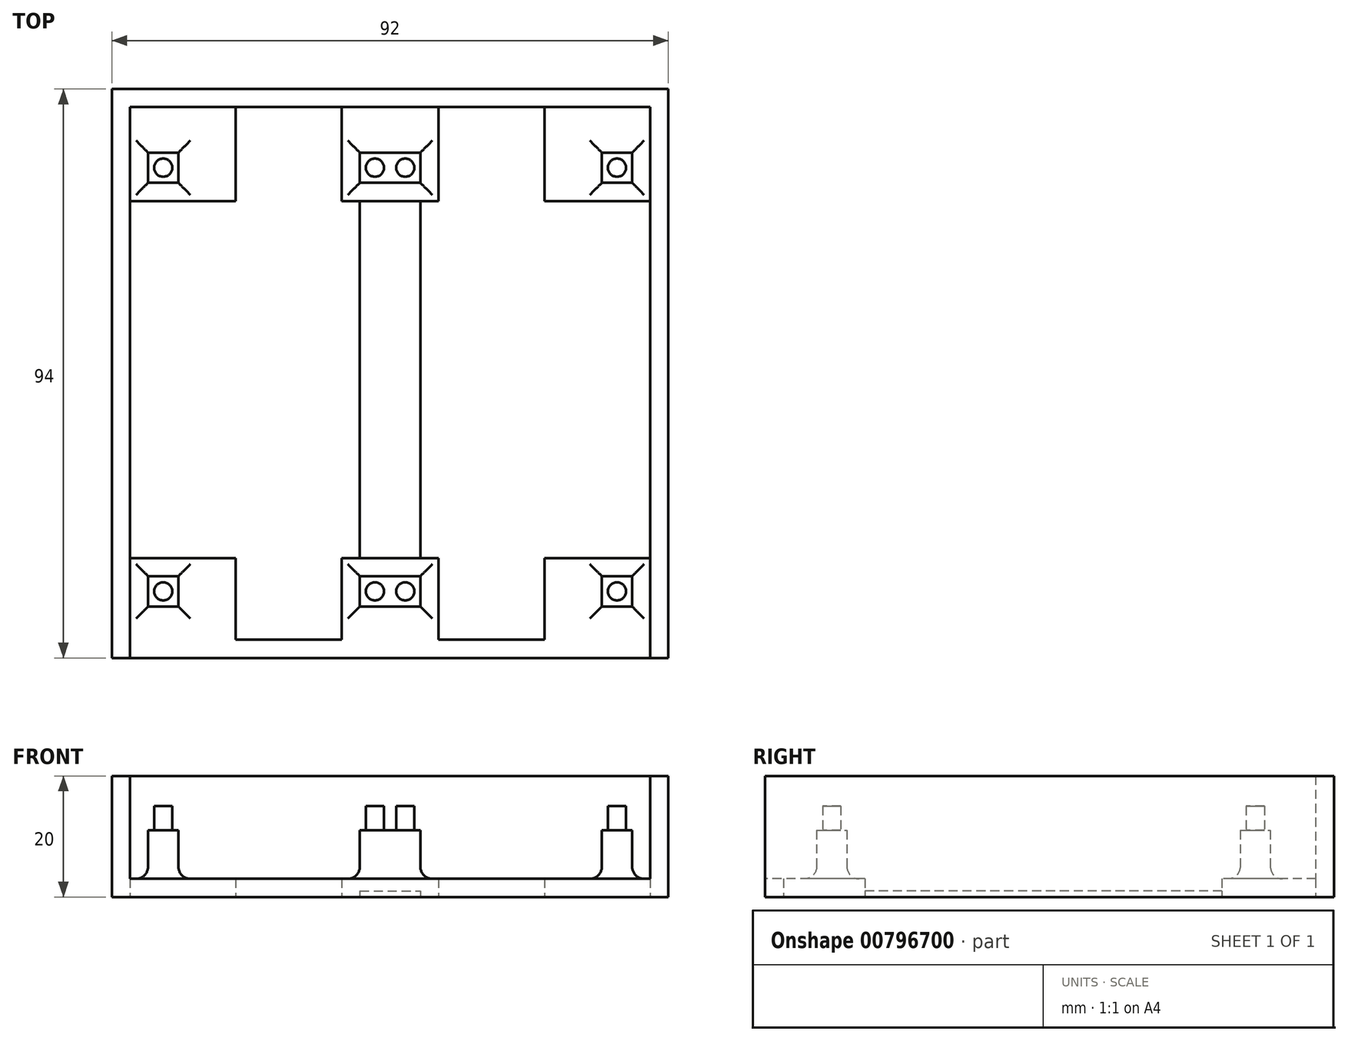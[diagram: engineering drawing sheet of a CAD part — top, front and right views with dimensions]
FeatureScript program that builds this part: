
annotation { "Feature Type Name" : "Feature", "Feature Type Description" : "" }
export const myFeature = defineFeature(function(context is Context, id is Id, definition is map)
    precondition{}
    {
        {
            var Q0;
            Q0=qCreatedBy(makeId("Top.planeOp"),FACE);
            var sketch = newSketch(context, id + "F0", { "sketchPlane" : qUnion([Q0])});
            skLineSegment(sketch, "E0.bottom", {"start": v(40, -41) * mm, "end": v(-40, -41) * mm, "construction": true});
            skLineSegment(sketch, "E0.top", {"start": v(40, 41) * mm, "end": v(-40, 41) * mm, "construction": true});
            skLineSegment(sketch, "E0.left", {"start": v(40, -41) * mm, "end": v(40, 41) * mm, "construction": true});
            skLineSegment(sketch, "E0.right", {"start": v(-40, -41) * mm, "end": v(-40, 41) * mm, "construction": true});
            skPoint(sketch, "E0.middle", {"position": v(0, 0) * mm});
            skLineSegment(sketch, "E1.bottom", {"start": v(-35, 31.5) * mm, "end": v(-40, 31.5) * mm});
            skLineSegment(sketch, "E1.top", {"start": v(-35, 36.5) * mm, "end": v(-40, 36.5) * mm});
            skLineSegment(sketch, "E1.left", {"start": v(-35, 31.5) * mm, "end": v(-35, 36.5) * mm});
            skLineSegment(sketch, "E1.right", {"start": v(-40, 31.5) * mm, "end": v(-40, 36.5) * mm});
            skPoint(sketch, "E1.middle", {"position": v(-37.5, 34) * mm});
            skLineSegment(sketch, "E2.bottom", {"start": v(-35, -38.5) * mm, "end": v(-40, -38.5) * mm});
            skLineSegment(sketch, "E2.top", {"start": v(-35, -33.5) * mm, "end": v(-40, -33.5) * mm});
            skLineSegment(sketch, "E2.left", {"start": v(-35, -38.5) * mm, "end": v(-35, -33.5) * mm});
            skLineSegment(sketch, "E2.right", {"start": v(-40, -38.5) * mm, "end": v(-40, -33.5) * mm});
            skPoint(sketch, "E2.middle", {"position": v(-37.5, -36) * mm});
            skLineSegment(sketch, "E3.bottom", {"start": v(40, -38.5) * mm, "end": v(35, -38.5) * mm});
            skLineSegment(sketch, "E3.top", {"start": v(40, -33.5) * mm, "end": v(35, -33.5) * mm});
            skLineSegment(sketch, "E3.left", {"start": v(40, -38.5) * mm, "end": v(40, -33.5) * mm});
            skLineSegment(sketch, "E3.right", {"start": v(35, -38.5) * mm, "end": v(35, -33.5) * mm});
            skPoint(sketch, "E3.middle", {"position": v(37.5, -36) * mm});
            skLineSegment(sketch, "E4.bottom", {"start": v(40, 31.5) * mm, "end": v(35, 31.5) * mm});
            skLineSegment(sketch, "E4.top", {"start": v(40, 36.5) * mm, "end": v(35, 36.5) * mm});
            skLineSegment(sketch, "E4.left", {"start": v(40, 31.5) * mm, "end": v(40, 36.5) * mm});
            skLineSegment(sketch, "E4.right", {"start": v(35, 31.5) * mm, "end": v(35, 36.5) * mm});
            skPoint(sketch, "E4.middle", {"position": v(37.5, 34) * mm});
            skLineSegment(sketch, "E5.bottom", {"start": v(0, 31.5) * mm, "end": v(-5, 31.5) * mm});
            skLineSegment(sketch, "E5.top", {"start": v(0, 36.5) * mm, "end": v(-5, 36.5) * mm});
            skLineSegment(sketch, "E5.left", {"start": v(0, 31.5) * mm, "end": v(0, 36.5) * mm});
            skLineSegment(sketch, "E5.right", {"start": v(-5, 31.5) * mm, "end": v(-5, 36.5) * mm});
            skPoint(sketch, "E5.middle", {"position": v(-2.5, 34) * mm});
            skLineSegment(sketch, "E6.bottom", {"start": v(0, -38.5) * mm, "end": v(-5, -38.5) * mm});
            skLineSegment(sketch, "E6.top", {"start": v(0, -33.5) * mm, "end": v(-5, -33.5) * mm});
            skLineSegment(sketch, "E6.left", {"start": v(0, -38.5) * mm, "end": v(0, -33.5) * mm});
            skLineSegment(sketch, "E6.right", {"start": v(-5, -38.5) * mm, "end": v(-5, -33.5) * mm});
            skPoint(sketch, "E6.middle", {"position": v(-2.5, -36) * mm});
            skLineSegment(sketch, "E7.bottom", {"start": v(5, -38.5) * mm, "end": v(0, -38.5) * mm});
            skLineSegment(sketch, "E7.top", {"start": v(5, -33.5) * mm, "end": v(0, -33.5) * mm});
            skLineSegment(sketch, "E7.left", {"start": v(5, -38.5) * mm, "end": v(5, -33.5) * mm});
            skPoint(sketch, "E7.middle", {"position": v(2.5, -36) * mm});
            skLineSegment(sketch, "E8", {"start": v(0, 41) * mm, "end": v(0, -41) * mm, "construction": true});
            skLineSegment(sketch, "E9.bottom", {"start": v(5, 31.5) * mm, "end": v(0, 31.5) * mm});
            skLineSegment(sketch, "E9.top", {"start": v(5, 36.5) * mm, "end": v(0, 36.5) * mm});
            skLineSegment(sketch, "E9.left", {"start": v(5, 31.5) * mm, "end": v(5, 36.5) * mm});
            skPoint(sketch, "E9.middle", {"position": v(2.5, 34) * mm});
            skPoint(sketch, "E9.middle.positionSnap0", {"position": v(0, 34) * mm});
            skPoint(sketch, "E9.centerSnap0", {"position": v(0, 34) * mm});
            skCircle(sketch, "E10", {"center": v(-37.5, 34) * mm, "radius": 1.5 * mm});
            skCircle(sketch, "E11", {"center": v(-2.5, 34) * mm, "radius": 1.5 * mm});
            skCircle(sketch, "E12", {"center": v(2.5, 34) * mm, "radius": 1.5 * mm});
            skCircle(sketch, "E13", {"center": v(37.5, 34) * mm, "radius": 1.5 * mm});
            skCircle(sketch, "E14", {"center": v(-37.5, -36) * mm, "radius": 1.5 * mm});
            skCircle(sketch, "E15", {"center": v(-2.5, -36) * mm, "radius": 1.5 * mm});
            skCircle(sketch, "E16", {"center": v(2.5, -36) * mm, "radius": 1.5 * mm});
            skCircle(sketch, "E17", {"center": v(37.5, -36) * mm, "radius": 1.5 * mm});
            skSolve(sketch);
        }
        {
            var Q0;
            Q0=qCreatedBy(makeId("Top.planeOp"),FACE);
            var sketch = newSketch(context, id + "F1", { "sketchPlane" : qUnion([Q0])});
            skLineSegment(sketch, "E18.0", {"start": v(40, 41) * mm, "end": v(-40, 41) * mm, "construction": true});
            skLineSegment(sketch, "E19.0", {"start": v(-40, -41) * mm, "end": v(-40, 41) * mm, "construction": true});
            skLineSegment(sketch, "E20.0", {"start": v(40, -41) * mm, "end": v(40, 41) * mm, "construction": true});
            skLineSegment(sketch, "E21.0", {"start": v(40, -41) * mm, "end": v(-40, -41) * mm, "construction": true});
            skLineSegment(sketch, "E22.bottom", {"start": v(43, -44) * mm, "end": v(-43, -44) * mm});
            skLineSegment(sketch, "E22.top", {"start": v(43, 44) * mm, "end": v(-43, 44) * mm});
            skLineSegment(sketch, "E22.left", {"start": v(43, -44) * mm, "end": v(43, 44) * mm});
            skLineSegment(sketch, "E22.right", {"start": v(-43, -44) * mm, "end": v(-43, 44) * mm});
            skPoint(sketch, "E22.middle", {"position": v(0, 0) * mm});
            skLineSegment(sketch, "E23.bottom", {"start": v(46, -47) * mm, "end": v(-46, -47) * mm});
            skLineSegment(sketch, "E23.top", {"start": v(46, 47) * mm, "end": v(-46, 47) * mm});
            skLineSegment(sketch, "E23.left", {"start": v(46, -47) * mm, "end": v(46, 47) * mm});
            skLineSegment(sketch, "E23.right", {"start": v(-46, -47) * mm, "end": v(-46, 47) * mm});
            skLineSegment(sketch, "E24", {"start": v(-43, -44) * mm, "end": v(-43, -47) * mm});
            skLineSegment(sketch, "E25", {"start": v(43, -44) * mm, "end": v(43, -47) * mm});
            skPoint(sketch, "E26.0", {"position": v(-37.5, 31.5) * mm});
            skPoint(sketch, "E27.0", {"position": v(-37.5, 36.5) * mm});
            skPoint(sketch, "E28.0", {"position": v(-37.5, -33.5) * mm});
            skPoint(sketch, "E29.0", {"position": v(-37.5, -38.5) * mm});
            skPoint(sketch, "E30.0", {"position": v(-5, 34) * mm});
            skPoint(sketch, "E31.0", {"position": v(5, 34) * mm});
            skLineSegment(sketch, "E32", {"start": v(-43, 31.5) * mm, "end": v(43, 31.5) * mm});
            skLineSegment(sketch, "E33", {"start": v(43, 36.5) * mm, "end": v(-43, 36.5) * mm});
            skLineSegment(sketch, "E34", {"start": v(-43, -33.5) * mm, "end": v(43, -33.5) * mm});
            skLineSegment(sketch, "E35", {"start": v(-43, -38.5) * mm, "end": v(43, -38.5) * mm});
            skLineSegment(sketch, "E36", {"start": v(-5, 44) * mm, "end": v(-5, -44) * mm});
            skLineSegment(sketch, "E37", {"start": v(5, 44) * mm, "end": v(5, -44) * mm});
            skLineSegment(sketch, "E38", {"start": v(-8, 44) * mm, "end": v(-8, -44) * mm});
            skLineSegment(sketch, "E39", {"start": v(8, 44) * mm, "end": v(8, -44) * mm});
            skLineSegment(sketch, "E40", {"start": v(-43, 28.5) * mm, "end": v(43, 28.5) * mm});
            skLineSegment(sketch, "E41", {"start": v(-43, -30.5) * mm, "end": v(43, -30.5) * mm});
            skPoint(sketch, "E42", {"position": v(-8, -30.5) * mm});
            skPoint(sketch, "E43", {"position": v(8, -30.5) * mm});
            skLineSegment(sketch, "E44", {"start": v(-8, -30.5) * mm, "end": v(-43, -30.5) * mm});
            skLineSegment(sketch, "E45", {"start": v(8, -30.5) * mm, "end": v(43, -30.5) * mm});
            skLineSegment(sketch, "E46", {"start": v(-25.5, -30.5) * mm, "end": v(-25.5, -44) * mm});
            skLineSegment(sketch, "E47", {"start": v(25.5, -30.5) * mm, "end": v(25.5, -44) * mm});
            skPoint(sketch, "E48", {"position": v(-8, 28.5) * mm});
            skPoint(sketch, "E49", {"position": v(8, 28.5) * mm});
            skLineSegment(sketch, "E50", {"start": v(-8, 28.5) * mm, "end": v(-43, 28.5) * mm});
            skLineSegment(sketch, "E51", {"start": v(8, 28.5) * mm, "end": v(43, 28.5) * mm});
            skLineSegment(sketch, "E52", {"start": v(-25.5, 28.5) * mm, "end": v(-25.5, 44) * mm});
            skLineSegment(sketch, "E53", {"start": v(25.5, 28.5) * mm, "end": v(25.5, 44) * mm});
            skLineSegment(sketch, "E54", {"start": v(-8, 28.5) * mm, "end": v(8, 28.5) * mm});
            skLineSegment(sketch, "E55", {"start": v(-8, -30.5) * mm, "end": v(8, -30.5) * mm});
            skSolve(sketch);
        }
        {
            var Q0;
            {var subQ0=sQuery(id+"F1.wireOp",EDGE,"E36");var subQ1=sQuery(id+"F1.wireOp",EDGE,"E22.bottom");var subQ2=makeQuery(id+"F1.imprint","INTERSECT",VERTEX,{"derivedFrom":[subQ1,subQ0]});Q0=makeQuery(id+"F1.imprint","IMPRINT",FACE,{"disambiguationData":[TD([[makeQuery(id+"F1.imprint","IMPRINT",EDGE,{"disambiguationData":[TD([[subQ2,-1.0]])],"derivedFrom":subQ1}),-1.0]])]});}
            var Q1;
            {var subQ0=sQuery(id+"F1.wireOp",EDGE,"E36");var subQ1=sQuery(id+"F1.wireOp",EDGE,"E22.top");var subQ2=makeQuery(id+"F1.imprint","INTERSECT",VERTEX,{"derivedFrom":[subQ1,subQ0]});Q1=makeQuery(id+"F1.imprint","IMPRINT",FACE,{"disambiguationData":[TD([[makeQuery(id+"F1.imprint","IMPRINT",EDGE,{"disambiguationData":[TD([[subQ2,-1.0]])],"derivedFrom":subQ1}),1.0]])]});}
            var Q2;
            {var subQ0=sQuery(id+"F1.wireOp",EDGE,"E38");var subQ1=sQuery(id+"F1.wireOp",EDGE,"E32");var subQ2=makeQuery(id+"F1.imprint","INTERSECT",VERTEX,{"derivedFrom":[subQ1,subQ0]});Q2=makeQuery(id+"F1.imprint","IMPRINT",FACE,{"disambiguationData":[TD([[makeQuery(id+"F1.imprint","IMPRINT",EDGE,{"disambiguationData":[TD([[subQ2,-1.0]])],"derivedFrom":subQ1}),1.0]])]});}
            var Q3;
            {var subQ0=sQuery(id+"F1.wireOp",EDGE,"E38");var subQ1=sQuery(id+"F1.wireOp",EDGE,"E32");var subQ2=makeQuery(id+"F1.imprint","INTERSECT",VERTEX,{"derivedFrom":[subQ1,subQ0]});Q3=makeQuery(id+"F1.imprint","IMPRINT",FACE,{"disambiguationData":[TD([[makeQuery(id+"F1.imprint","IMPRINT",EDGE,{"disambiguationData":[TD([[subQ2,-1.0]])],"derivedFrom":subQ1}),-1.0]])]});}
            var Q4;
            {var subQ0=sQuery(id+"F1.wireOp",EDGE,"E38");var subQ1=sQuery(id+"F1.wireOp",EDGE,"E34");var subQ2=makeQuery(id+"F1.imprint","INTERSECT",VERTEX,{"derivedFrom":[subQ1,subQ0]});Q4=makeQuery(id+"F1.imprint","IMPRINT",FACE,{"disambiguationData":[TD([[makeQuery(id+"F1.imprint","IMPRINT",EDGE,{"disambiguationData":[TD([[subQ2,-1.0]])],"derivedFrom":subQ1}),-1.0]])]});}
            var Q5;
            {var subQ0=sQuery(id+"F1.wireOp",EDGE,"E38");var subQ1=sQuery(id+"F1.wireOp",EDGE,"E34");var subQ2=makeQuery(id+"F1.imprint","INTERSECT",VERTEX,{"derivedFrom":[subQ1,subQ0]});Q5=makeQuery(id+"F1.imprint","IMPRINT",FACE,{"disambiguationData":[TD([[makeQuery(id+"F1.imprint","IMPRINT",EDGE,{"disambiguationData":[TD([[subQ2,-1.0]])],"derivedFrom":subQ1}),1.0]])]});}
            var Q6;
            {var subQ6=sQuery(id+"F1.wireOp",EDGE,"E24");Q6=makeQuery(id+"F1.imprint","IMPRINT",FACE,{"disambiguationData":[TD([[makeQuery(id+"F1.imprint","IMPRINT",EDGE,{"derivedFrom":subQ6}),1.0]])]});}
            var Q7;
            Q7=makeQuery(id+"F1.imprint","IMPRINT",FACE,{"disambiguationData":[TD([[makeQuery(id+"F1.imprint","IMPRINT",EDGE,{"derivedFrom":sQuery(id+"F1.wireOp",EDGE,"E23.top")}),1.0]])]});
            var Q8;
            {var subQ0=sQuery(id+"F1.wireOp",EDGE,"E22.right");var subQ1=sQuery(id+"F1.wireOp",EDGE,"E22.top");var subQ2=makeQuery(id+"F1.imprint","INTERSECT",VERTEX,{"derivedFrom":[subQ1,subQ0]});Q8=makeQuery(id+"F1.imprint","IMPRINT",FACE,{"disambiguationData":[TD([[makeQuery(id+"F1.imprint","IMPRINT",EDGE,{"disambiguationData":[TD([[subQ2,1.0]])],"derivedFrom":subQ1}),1.0]])]});}
            var Q9;
            {var subQ0=sQuery(id+"F1.wireOp",EDGE,"E36");var subQ1=sQuery(id+"F1.wireOp",EDGE,"E22.top");var subQ2=makeQuery(id+"F1.imprint","INTERSECT",VERTEX,{"derivedFrom":[subQ1,subQ0]});Q9=makeQuery(id+"F1.imprint","IMPRINT",FACE,{"disambiguationData":[TD([[makeQuery(id+"F1.imprint","IMPRINT",EDGE,{"disambiguationData":[TD([[subQ2,1.0]])],"derivedFrom":subQ1}),1.0]])]});}
            var Q10;
            {var subQ0=sQuery(id+"F1.wireOp",EDGE,"E37");var subQ1=sQuery(id+"F1.wireOp",EDGE,"E22.top");var subQ2=makeQuery(id+"F1.imprint","INTERSECT",VERTEX,{"derivedFrom":[subQ1,subQ0]});Q10=makeQuery(id+"F1.imprint","IMPRINT",FACE,{"disambiguationData":[TD([[makeQuery(id+"F1.imprint","IMPRINT",EDGE,{"disambiguationData":[TD([[subQ2,1.0]])],"derivedFrom":subQ1}),1.0]])]});}
            var Q11;
            {var subQ0=sQuery(id+"F1.wireOp",EDGE,"E22.left");var subQ1=sQuery(id+"F1.wireOp",EDGE,"E22.top");var subQ2=makeQuery(id+"F1.imprint","INTERSECT",VERTEX,{"derivedFrom":[subQ1,subQ0]});Q11=makeQuery(id+"F1.imprint","IMPRINT",FACE,{"disambiguationData":[TD([[makeQuery(id+"F1.imprint","IMPRINT",EDGE,{"disambiguationData":[TD([[subQ2,-1.0]])],"derivedFrom":subQ1}),1.0]])]});}
            var Q12;
            {var subQ0=sQuery(id+"F1.wireOp",EDGE,"E32");var subQ1=sQuery(id+"F1.wireOp",EDGE,"E22.left");var subQ2=makeQuery(id+"F1.imprint","INTERSECT",VERTEX,{"derivedFrom":[subQ1,subQ0]});Q12=makeQuery(id+"F1.imprint","IMPRINT",FACE,{"disambiguationData":[TD([[makeQuery(id+"F1.imprint","IMPRINT",EDGE,{"disambiguationData":[TD([[subQ2,-1.0]])],"derivedFrom":subQ1}),1.0]])]});}
            var Q13;
            {var subQ0=sQuery(id+"F1.wireOp",EDGE,"E37");var subQ1=sQuery(id+"F1.wireOp",EDGE,"E32");var subQ2=makeQuery(id+"F1.imprint","INTERSECT",VERTEX,{"derivedFrom":[subQ1,subQ0]});Q13=makeQuery(id+"F1.imprint","IMPRINT",FACE,{"disambiguationData":[TD([[makeQuery(id+"F1.imprint","IMPRINT",EDGE,{"disambiguationData":[TD([[subQ2,-1.0]])],"derivedFrom":subQ1}),1.0]])]});}
            var Q14;
            {var subQ0=sQuery(id+"F1.wireOp",EDGE,"E32");var subQ1=sQuery(id+"F1.wireOp",EDGE,"E22.right");var subQ2=makeQuery(id+"F1.imprint","INTERSECT",VERTEX,{"derivedFrom":[subQ1,subQ0]});Q14=makeQuery(id+"F1.imprint","IMPRINT",FACE,{"disambiguationData":[TD([[makeQuery(id+"F1.imprint","IMPRINT",EDGE,{"disambiguationData":[TD([[subQ2,-1.0]])],"derivedFrom":subQ1}),-1.0]])]});}
            var Q15;
            {var subQ0=sQuery(id+"F1.wireOp",EDGE,"E36");var subQ1=sQuery(id+"F1.wireOp",EDGE,"E32");var subQ2=makeQuery(id+"F1.imprint","INTERSECT",VERTEX,{"derivedFrom":[subQ1,subQ0]});Q15=makeQuery(id+"F1.imprint","IMPRINT",FACE,{"disambiguationData":[TD([[makeQuery(id+"F1.imprint","IMPRINT",EDGE,{"disambiguationData":[TD([[subQ2,-1.0]])],"derivedFrom":subQ1}),1.0]])]});}
            var Q16;
            {var subQ0=sQuery(id+"F1.wireOp",EDGE,"E32");var subQ1=sQuery(id+"F1.wireOp",EDGE,"E22.right");var subQ2=makeQuery(id+"F1.imprint","INTERSECT",VERTEX,{"derivedFrom":[subQ1,subQ0]});Q16=makeQuery(id+"F1.imprint","IMPRINT",FACE,{"disambiguationData":[TD([[makeQuery(id+"F1.imprint","IMPRINT",EDGE,{"disambiguationData":[TD([[subQ2,1.0]])],"derivedFrom":subQ1}),-1.0]])]});}
            var Q17;
            {var subQ0=sQuery(id+"F1.wireOp",EDGE,"E37");var subQ1=sQuery(id+"F1.wireOp",EDGE,"E32");var subQ2=makeQuery(id+"F1.imprint","INTERSECT",VERTEX,{"derivedFrom":[subQ1,subQ0]});Q17=makeQuery(id+"F1.imprint","IMPRINT",FACE,{"disambiguationData":[TD([[makeQuery(id+"F1.imprint","IMPRINT",EDGE,{"disambiguationData":[TD([[subQ2,-1.0]])],"derivedFrom":subQ1}),-1.0]])]});}
            var Q18;
            {var subQ0=sQuery(id+"F1.wireOp",EDGE,"E32");var subQ1=sQuery(id+"F1.wireOp",EDGE,"E22.left");var subQ2=makeQuery(id+"F1.imprint","INTERSECT",VERTEX,{"derivedFrom":[subQ1,subQ0]});Q18=makeQuery(id+"F1.imprint","IMPRINT",FACE,{"disambiguationData":[TD([[makeQuery(id+"F1.imprint","IMPRINT",EDGE,{"disambiguationData":[TD([[subQ2,1.0]])],"derivedFrom":subQ1}),1.0]])]});}
            var Q19;
            {var subQ0=sQuery(id+"F1.wireOp",EDGE,"E36");var subQ1=sQuery(id+"F1.wireOp",EDGE,"E32");var subQ2=makeQuery(id+"F1.imprint","INTERSECT",VERTEX,{"derivedFrom":[subQ1,subQ0]});Q19=makeQuery(id+"F1.imprint","IMPRINT",FACE,{"disambiguationData":[TD([[makeQuery(id+"F1.imprint","IMPRINT",EDGE,{"disambiguationData":[TD([[subQ2,-1.0]])],"derivedFrom":subQ1}),-1.0]])]});}
            var Q20;
            {var subQ0=sQuery(id+"F1.wireOp",EDGE,"E36");var subQ1=sQuery(id+"F1.wireOp",EDGE,"E22.bottom");var subQ2=makeQuery(id+"F1.imprint","INTERSECT",VERTEX,{"derivedFrom":[subQ1,subQ0]});Q20=makeQuery(id+"F1.imprint","IMPRINT",FACE,{"disambiguationData":[TD([[makeQuery(id+"F1.imprint","IMPRINT",EDGE,{"disambiguationData":[TD([[subQ2,1.0]])],"derivedFrom":subQ1}),-1.0]])]});}
            var Q21;
            {var subQ0=sQuery(id+"F1.wireOp",EDGE,"E36");var subQ1=sQuery(id+"F1.wireOp",EDGE,"E34");var subQ2=makeQuery(id+"F1.imprint","INTERSECT",VERTEX,{"derivedFrom":[subQ1,subQ0]});Q21=makeQuery(id+"F1.imprint","IMPRINT",FACE,{"disambiguationData":[TD([[makeQuery(id+"F1.imprint","IMPRINT",EDGE,{"disambiguationData":[TD([[subQ2,-1.0]])],"derivedFrom":subQ1}),-1.0]])]});}
            var Q22;
            {var subQ0=sQuery(id+"F1.wireOp",EDGE,"E36");var subQ1=sQuery(id+"F1.wireOp",EDGE,"E34");var subQ2=makeQuery(id+"F1.imprint","INTERSECT",VERTEX,{"derivedFrom":[subQ1,subQ0]});Q22=makeQuery(id+"F1.imprint","IMPRINT",FACE,{"disambiguationData":[TD([[makeQuery(id+"F1.imprint","IMPRINT",EDGE,{"disambiguationData":[TD([[subQ2,-1.0]])],"derivedFrom":subQ1}),1.0]])]});}
            var Q23;
            {var subQ0=sQuery(id+"F1.wireOp",EDGE,"E37");var subQ1=sQuery(id+"F1.wireOp",EDGE,"E22.bottom");var subQ2=makeQuery(id+"F1.imprint","INTERSECT",VERTEX,{"derivedFrom":[subQ1,subQ0]});Q23=makeQuery(id+"F1.imprint","IMPRINT",FACE,{"disambiguationData":[TD([[makeQuery(id+"F1.imprint","IMPRINT",EDGE,{"disambiguationData":[TD([[subQ2,1.0]])],"derivedFrom":subQ1}),-1.0]])]});}
            var Q24;
            {var subQ0=sQuery(id+"F1.wireOp",EDGE,"E37");var subQ1=sQuery(id+"F1.wireOp",EDGE,"E34");var subQ2=makeQuery(id+"F1.imprint","INTERSECT",VERTEX,{"derivedFrom":[subQ1,subQ0]});Q24=makeQuery(id+"F1.imprint","IMPRINT",FACE,{"disambiguationData":[TD([[makeQuery(id+"F1.imprint","IMPRINT",EDGE,{"disambiguationData":[TD([[subQ2,-1.0]])],"derivedFrom":subQ1}),-1.0]])]});}
            var Q25;
            {var subQ0=sQuery(id+"F1.wireOp",EDGE,"E37");var subQ1=sQuery(id+"F1.wireOp",EDGE,"E34");var subQ2=makeQuery(id+"F1.imprint","INTERSECT",VERTEX,{"derivedFrom":[subQ1,subQ0]});Q25=makeQuery(id+"F1.imprint","IMPRINT",FACE,{"disambiguationData":[TD([[makeQuery(id+"F1.imprint","IMPRINT",EDGE,{"disambiguationData":[TD([[subQ2,-1.0]])],"derivedFrom":subQ1}),1.0]])]});}
            var Q26;
            {var subQ0=sQuery(id+"F1.wireOp",EDGE,"E34");var subQ1=sQuery(id+"F1.wireOp",EDGE,"E22.right");var subQ2=makeQuery(id+"F1.imprint","INTERSECT",VERTEX,{"derivedFrom":[subQ1,subQ0]});Q26=makeQuery(id+"F1.imprint","IMPRINT",FACE,{"disambiguationData":[TD([[makeQuery(id+"F1.imprint","IMPRINT",EDGE,{"disambiguationData":[TD([[subQ2,-1.0]])],"derivedFrom":subQ1}),-1.0]])]});}
            var Q27;
            {var subQ0=sQuery(id+"F1.wireOp",EDGE,"E34");var subQ1=sQuery(id+"F1.wireOp",EDGE,"E22.left");var subQ2=makeQuery(id+"F1.imprint","INTERSECT",VERTEX,{"derivedFrom":[subQ1,subQ0]});Q27=makeQuery(id+"F1.imprint","IMPRINT",FACE,{"disambiguationData":[TD([[makeQuery(id+"F1.imprint","IMPRINT",EDGE,{"disambiguationData":[TD([[subQ2,-1.0]])],"derivedFrom":subQ1}),1.0]])]});}
            var Q28;
            {var subQ0=sQuery(id+"F1.wireOp",EDGE,"E34");var subQ1=sQuery(id+"F1.wireOp",EDGE,"E22.left");var subQ2=makeQuery(id+"F1.imprint","INTERSECT",VERTEX,{"derivedFrom":[subQ1,subQ0]});Q28=makeQuery(id+"F1.imprint","IMPRINT",FACE,{"disambiguationData":[TD([[makeQuery(id+"F1.imprint","IMPRINT",EDGE,{"disambiguationData":[TD([[subQ2,1.0]])],"derivedFrom":subQ1}),1.0]])]});}
            var Q29;
            {var subQ0=sQuery(id+"F1.wireOp",EDGE,"E34");var subQ1=sQuery(id+"F1.wireOp",EDGE,"E22.right");var subQ2=makeQuery(id+"F1.imprint","INTERSECT",VERTEX,{"derivedFrom":[subQ1,subQ0]});Q29=makeQuery(id+"F1.imprint","IMPRINT",FACE,{"disambiguationData":[TD([[makeQuery(id+"F1.imprint","IMPRINT",EDGE,{"disambiguationData":[TD([[subQ2,1.0]])],"derivedFrom":subQ1}),-1.0]])]});}
            var Q30;
            {var subQ0=sQuery(id+"F1.wireOp",EDGE,"E22.right");var subQ5=sQuery(id+"F1.wireOp",EDGE,"E35");var subQ6=makeQuery(id+"F1.imprint","INTERSECT",VERTEX,{"derivedFrom":[subQ0,subQ5]});Q30=makeQuery(id+"F1.imprint","IMPRINT",FACE,{"disambiguationData":[TD([[makeQuery(id+"F1.imprint","IMPRINT",EDGE,{"disambiguationData":[TD([[subQ6,-1.0]])],"derivedFrom":subQ5}),-1.0]])]});}
            var Q31;
            {var subQ0=sQuery(id+"F1.wireOp",EDGE,"E22.left");var subQ5=sQuery(id+"F1.wireOp",EDGE,"E35");var subQ6=makeQuery(id+"F1.imprint","INTERSECT",VERTEX,{"derivedFrom":[subQ0,subQ5]});Q31=makeQuery(id+"F1.imprint","IMPRINT",FACE,{"disambiguationData":[TD([[makeQuery(id+"F1.imprint","IMPRINT",EDGE,{"disambiguationData":[TD([[subQ6,1.0]])],"derivedFrom":subQ5}),-1.0]])]});}
            extrude(context, id + "F2", {"entities" : qUnion([Q0, Q1, Q2, Q3, Q4, Q5, Q6, Q7, Q8, Q9, Q10, Q11, Q12, Q13, Q14, Q15, Q16, Q17, Q18, Q19, Q20, Q21, Q22, Q23, Q24, Q25, Q26, Q27, Q28, Q29, Q30, Q31]), "depth" : 3 * mm, "offsetDistance" : 25 * mm});
        }
        {
            var Q0;
            Q0=makeQuery(id+"F1.imprint","IMPRINT",FACE,{"disambiguationData":[TD([[makeQuery(id+"F1.imprint","IMPRINT",EDGE,{"derivedFrom":sQuery(id+"F1.wireOp",EDGE,"E23.top")}),1.0]])]});
            extrude(context, id + "F3", {"entities" : qUnion([Q0]), "operationType" : NewBodyOperationType.ADD, "depth" : 20 * mm, "offsetDistance" : 25 * mm});
        }
        {
            var Q0;
            Q0=makeQuery(id+"F0.imprint","IMPRINT",FACE,{"disambiguationData":[TD([[makeQuery(id+"F0.imprint","IMPRINT",EDGE,{"derivedFrom":sQuery(id+"F0.wireOp",EDGE,"E4.bottom")}),-1.0]])]});
            var Q1;
            Q1=makeQuery(id+"F0.imprint","IMPRINT",FACE,{"disambiguationData":[TD([[makeQuery(id+"F0.imprint","IMPRINT",EDGE,{"derivedFrom":sQuery(id+"F0.wireOp",EDGE,"E13")}),1.0]])]});
            var Q2;
            Q2=makeQuery(id+"F0.imprint","IMPRINT",FACE,{"disambiguationData":[TD([[makeQuery(id+"F0.imprint","IMPRINT",EDGE,{"derivedFrom":sQuery(id+"F0.wireOp",EDGE,"E9.bottom")}),-1.0]])]});
            var Q3;
            Q3=makeQuery(id+"F0.imprint","IMPRINT",FACE,{"disambiguationData":[TD([[makeQuery(id+"F0.imprint","IMPRINT",EDGE,{"derivedFrom":sQuery(id+"F0.wireOp",EDGE,"E12")}),1.0]])]});
            var Q4;
            Q4=makeQuery(id+"F0.imprint","IMPRINT",FACE,{"disambiguationData":[TD([[makeQuery(id+"F0.imprint","IMPRINT",EDGE,{"derivedFrom":sQuery(id+"F0.wireOp",EDGE,"E5.bottom")}),-1.0]])]});
            var Q5;
            Q5=makeQuery(id+"F0.imprint","IMPRINT",FACE,{"disambiguationData":[TD([[makeQuery(id+"F0.imprint","IMPRINT",EDGE,{"derivedFrom":sQuery(id+"F0.wireOp",EDGE,"E11")}),1.0]])]});
            var Q6;
            Q6=makeQuery(id+"F0.imprint","IMPRINT",FACE,{"disambiguationData":[TD([[makeQuery(id+"F0.imprint","IMPRINT",EDGE,{"derivedFrom":sQuery(id+"F0.wireOp",EDGE,"E1.bottom")}),-1.0]])]});
            var Q7;
            Q7=makeQuery(id+"F0.imprint","IMPRINT",FACE,{"disambiguationData":[TD([[makeQuery(id+"F0.imprint","IMPRINT",EDGE,{"derivedFrom":sQuery(id+"F0.wireOp",EDGE,"E10")}),1.0]])]});
            var Q8;
            Q8=makeQuery(id+"F0.imprint","IMPRINT",FACE,{"disambiguationData":[TD([[makeQuery(id+"F0.imprint","IMPRINT",EDGE,{"derivedFrom":sQuery(id+"F0.wireOp",EDGE,"E17")}),1.0]])]});
            var Q9;
            Q9=makeQuery(id+"F0.imprint","IMPRINT",FACE,{"disambiguationData":[TD([[makeQuery(id+"F0.imprint","IMPRINT",EDGE,{"derivedFrom":sQuery(id+"F0.wireOp",EDGE,"E3.bottom")}),-1.0]])]});
            var Q10;
            Q10=makeQuery(id+"F0.imprint","IMPRINT",FACE,{"disambiguationData":[TD([[makeQuery(id+"F0.imprint","IMPRINT",EDGE,{"derivedFrom":sQuery(id+"F0.wireOp",EDGE,"E6.bottom")}),-1.0]])]});
            var Q11;
            Q11=makeQuery(id+"F0.imprint","IMPRINT",FACE,{"disambiguationData":[TD([[makeQuery(id+"F0.imprint","IMPRINT",EDGE,{"derivedFrom":sQuery(id+"F0.wireOp",EDGE,"E15")}),1.0]])]});
            var Q12;
            Q12=makeQuery(id+"F0.imprint","IMPRINT",FACE,{"disambiguationData":[TD([[makeQuery(id+"F0.imprint","IMPRINT",EDGE,{"derivedFrom":sQuery(id+"F0.wireOp",EDGE,"E7.bottom")}),-1.0]])]});
            var Q13;
            Q13=makeQuery(id+"F0.imprint","IMPRINT",FACE,{"disambiguationData":[TD([[makeQuery(id+"F0.imprint","IMPRINT",EDGE,{"derivedFrom":sQuery(id+"F0.wireOp",EDGE,"E16")}),1.0]])]});
            var Q14;
            Q14=makeQuery(id+"F0.imprint","IMPRINT",FACE,{"disambiguationData":[TD([[makeQuery(id+"F0.imprint","IMPRINT",EDGE,{"derivedFrom":sQuery(id+"F0.wireOp",EDGE,"E2.bottom")}),-1.0]])]});
            var Q15;
            Q15=makeQuery(id+"F0.imprint","IMPRINT",FACE,{"disambiguationData":[TD([[makeQuery(id+"F0.imprint","IMPRINT",EDGE,{"derivedFrom":sQuery(id+"F0.wireOp",EDGE,"E14")}),1.0]])]});
            extrude(context, id + "F4", {"entities" : qUnion([Q0, Q1, Q2, Q3, Q4, Q5, Q6, Q7, Q8, Q9, Q10, Q11, Q12, Q13, Q14, Q15]), "operationType" : NewBodyOperationType.ADD, "depth" : 11 * mm, "offsetDistance" : 25 * mm});
        }
        {
            var Q0;
            Q0=makeQuery(id+"F0.imprint","IMPRINT",FACE,{"disambiguationData":[TD([[makeQuery(id+"F0.imprint","IMPRINT",EDGE,{"derivedFrom":sQuery(id+"F0.wireOp",EDGE,"E17")}),1.0]])]});
            var Q1;
            Q1=makeQuery(id+"F0.imprint","IMPRINT",FACE,{"disambiguationData":[TD([[makeQuery(id+"F0.imprint","IMPRINT",EDGE,{"derivedFrom":sQuery(id+"F0.wireOp",EDGE,"E16")}),1.0]])]});
            var Q2;
            Q2=makeQuery(id+"F0.imprint","IMPRINT",FACE,{"disambiguationData":[TD([[makeQuery(id+"F0.imprint","IMPRINT",EDGE,{"derivedFrom":sQuery(id+"F0.wireOp",EDGE,"E15")}),1.0]])]});
            var Q3;
            Q3=makeQuery(id+"F0.imprint","IMPRINT",FACE,{"disambiguationData":[TD([[makeQuery(id+"F0.imprint","IMPRINT",EDGE,{"derivedFrom":sQuery(id+"F0.wireOp",EDGE,"E14")}),1.0]])]});
            var Q4;
            Q4=makeQuery(id+"F0.imprint","IMPRINT",FACE,{"disambiguationData":[TD([[makeQuery(id+"F0.imprint","IMPRINT",EDGE,{"derivedFrom":sQuery(id+"F0.wireOp",EDGE,"E10")}),1.0]])]});
            var Q5;
            Q5=makeQuery(id+"F0.imprint","IMPRINT",FACE,{"disambiguationData":[TD([[makeQuery(id+"F0.imprint","IMPRINT",EDGE,{"derivedFrom":sQuery(id+"F0.wireOp",EDGE,"E11")}),1.0]])]});
            var Q6;
            Q6=makeQuery(id+"F0.imprint","IMPRINT",FACE,{"disambiguationData":[TD([[makeQuery(id+"F0.imprint","IMPRINT",EDGE,{"derivedFrom":sQuery(id+"F0.wireOp",EDGE,"E12")}),1.0]])]});
            var Q7;
            Q7=makeQuery(id+"F0.imprint","IMPRINT",FACE,{"disambiguationData":[TD([[makeQuery(id+"F0.imprint","IMPRINT",EDGE,{"derivedFrom":sQuery(id+"F0.wireOp",EDGE,"E13")}),1.0]])]});
            extrude(context, id + "F5", {"entities" : qUnion([Q0, Q1, Q2, Q3, Q4, Q5, Q6, Q7]), "operationType" : NewBodyOperationType.ADD, "depth" : 15 * mm, "offsetDistance" : 25 * mm});
        }
        {
            var Q0;
            Q0=makeQuery(id+"F4.boolean.opBoolean","INTERSECT",EDGE,{"derivedFrom":[makeQuery(id+"F2.opExtrude","CAP_FACE",FACE,{"disambiguationData":[OSD([sQuery(id+"F1.wireOp",EDGE,"E22.left"),sQuery(id+"F1.wireOp",EDGE,"E22.right"),sQuery(id+"F1.wireOp",EDGE,"E23.bottom"),sQuery(id+"F1.wireOp",EDGE,"E23.top"),sQuery(id+"F1.wireOp",EDGE,"E23.left"),sQuery(id+"F1.wireOp",EDGE,"E23.right"),sQuery(id+"F1.wireOp",EDGE,"E38"),sQuery(id+"F1.wireOp",EDGE,"E39"),sQuery(id+"F1.wireOp",EDGE,"E40"),sQuery(id+"F1.wireOp",EDGE,"E41")])],"isStart":false}),makeQuery(id+"F4.opExtrude","SWEPT_FACE",FACE,{"disambiguationData":[OSD([sQuery(id+"F0.wireOp",EDGE,"E2.bottom")])]})]});
            var Q1;
            Q1=makeQuery(id+"F4.boolean.opBoolean","INTERSECT",EDGE,{"derivedFrom":[makeQuery(id+"F2.opExtrude","CAP_FACE",FACE,{"disambiguationData":[OSD([sQuery(id+"F1.wireOp",EDGE,"E22.left"),sQuery(id+"F1.wireOp",EDGE,"E22.right"),sQuery(id+"F1.wireOp",EDGE,"E23.bottom"),sQuery(id+"F1.wireOp",EDGE,"E23.top"),sQuery(id+"F1.wireOp",EDGE,"E23.left"),sQuery(id+"F1.wireOp",EDGE,"E23.right"),sQuery(id+"F1.wireOp",EDGE,"E38"),sQuery(id+"F1.wireOp",EDGE,"E39"),sQuery(id+"F1.wireOp",EDGE,"E40"),sQuery(id+"F1.wireOp",EDGE,"E41")])],"isStart":false}),makeQuery(id+"F4.opExtrude","SWEPT_FACE",FACE,{"disambiguationData":[OSD([sQuery(id+"F0.wireOp",EDGE,"E2.left")])]})]});
            var Q2;
            Q2=makeQuery(id+"F4.boolean.opBoolean","INTERSECT",EDGE,{"derivedFrom":[makeQuery(id+"F2.opExtrude","CAP_FACE",FACE,{"disambiguationData":[OSD([sQuery(id+"F1.wireOp",EDGE,"E22.left"),sQuery(id+"F1.wireOp",EDGE,"E22.right"),sQuery(id+"F1.wireOp",EDGE,"E23.bottom"),sQuery(id+"F1.wireOp",EDGE,"E23.top"),sQuery(id+"F1.wireOp",EDGE,"E23.left"),sQuery(id+"F1.wireOp",EDGE,"E23.right"),sQuery(id+"F1.wireOp",EDGE,"E38"),sQuery(id+"F1.wireOp",EDGE,"E39"),sQuery(id+"F1.wireOp",EDGE,"E40"),sQuery(id+"F1.wireOp",EDGE,"E41")])],"isStart":false}),makeQuery(id+"F4.opExtrude","SWEPT_FACE",FACE,{"disambiguationData":[OSD([sQuery(id+"F0.wireOp",EDGE,"E2.top")])]})]});
            var Q3;
            Q3=makeQuery(id+"F4.boolean.opBoolean","INTERSECT",EDGE,{"derivedFrom":[makeQuery(id+"F2.opExtrude","CAP_FACE",FACE,{"disambiguationData":[OSD([sQuery(id+"F1.wireOp",EDGE,"E22.left"),sQuery(id+"F1.wireOp",EDGE,"E22.right"),sQuery(id+"F1.wireOp",EDGE,"E23.bottom"),sQuery(id+"F1.wireOp",EDGE,"E23.top"),sQuery(id+"F1.wireOp",EDGE,"E23.left"),sQuery(id+"F1.wireOp",EDGE,"E23.right"),sQuery(id+"F1.wireOp",EDGE,"E38"),sQuery(id+"F1.wireOp",EDGE,"E39"),sQuery(id+"F1.wireOp",EDGE,"E40"),sQuery(id+"F1.wireOp",EDGE,"E41")])],"isStart":false}),makeQuery(id+"F4.opExtrude","SWEPT_FACE",FACE,{"disambiguationData":[OSD([sQuery(id+"F0.wireOp",EDGE,"E2.right")])]})]});
            var Q4;
            Q4=makeQuery(id+"F4.boolean.opBoolean","INTERSECT",EDGE,{"derivedFrom":[makeQuery(id+"F2.opExtrude","CAP_FACE",FACE,{"disambiguationData":[OSD([sQuery(id+"F1.wireOp",EDGE,"E22.left"),sQuery(id+"F1.wireOp",EDGE,"E22.right"),sQuery(id+"F1.wireOp",EDGE,"E23.bottom"),sQuery(id+"F1.wireOp",EDGE,"E23.top"),sQuery(id+"F1.wireOp",EDGE,"E23.left"),sQuery(id+"F1.wireOp",EDGE,"E23.right"),sQuery(id+"F1.wireOp",EDGE,"E38"),sQuery(id+"F1.wireOp",EDGE,"E39"),sQuery(id+"F1.wireOp",EDGE,"E40"),sQuery(id+"F1.wireOp",EDGE,"E41")])],"isStart":false}),makeQuery(id+"F4.opExtrude","SWEPT_FACE",FACE,{"disambiguationData":[OSD([sQuery(id+"F0.wireOp",EDGE,"E6.bottom"),sQuery(id+"F0.wireOp",EDGE,"E7.bottom")])]})]});
            var Q5;
            Q5=makeQuery(id+"F4.boolean.opBoolean","INTERSECT",EDGE,{"derivedFrom":[makeQuery(id+"F2.opExtrude","CAP_FACE",FACE,{"disambiguationData":[OSD([sQuery(id+"F1.wireOp",EDGE,"E22.left"),sQuery(id+"F1.wireOp",EDGE,"E22.right"),sQuery(id+"F1.wireOp",EDGE,"E23.bottom"),sQuery(id+"F1.wireOp",EDGE,"E23.top"),sQuery(id+"F1.wireOp",EDGE,"E23.left"),sQuery(id+"F1.wireOp",EDGE,"E23.right"),sQuery(id+"F1.wireOp",EDGE,"E38"),sQuery(id+"F1.wireOp",EDGE,"E39"),sQuery(id+"F1.wireOp",EDGE,"E40"),sQuery(id+"F1.wireOp",EDGE,"E41")])],"isStart":false}),makeQuery(id+"F4.opExtrude","SWEPT_FACE",FACE,{"disambiguationData":[OSD([sQuery(id+"F0.wireOp",EDGE,"E1.bottom")])]})]});
            var Q6;
            Q6=makeQuery(id+"F4.boolean.opBoolean","INTERSECT",EDGE,{"derivedFrom":[makeQuery(id+"F2.opExtrude","CAP_FACE",FACE,{"disambiguationData":[OSD([sQuery(id+"F1.wireOp",EDGE,"E22.left"),sQuery(id+"F1.wireOp",EDGE,"E22.right"),sQuery(id+"F1.wireOp",EDGE,"E23.bottom"),sQuery(id+"F1.wireOp",EDGE,"E23.top"),sQuery(id+"F1.wireOp",EDGE,"E23.left"),sQuery(id+"F1.wireOp",EDGE,"E23.right"),sQuery(id+"F1.wireOp",EDGE,"E38"),sQuery(id+"F1.wireOp",EDGE,"E39"),sQuery(id+"F1.wireOp",EDGE,"E40"),sQuery(id+"F1.wireOp",EDGE,"E41")])],"isStart":false}),makeQuery(id+"F4.opExtrude","SWEPT_FACE",FACE,{"disambiguationData":[OSD([sQuery(id+"F0.wireOp",EDGE,"E5.bottom"),sQuery(id+"F0.wireOp",EDGE,"E9.bottom")])]})]});
            var Q7;
            Q7=makeQuery(id+"F4.boolean.opBoolean","INTERSECT",EDGE,{"derivedFrom":[makeQuery(id+"F2.opExtrude","CAP_FACE",FACE,{"disambiguationData":[OSD([sQuery(id+"F1.wireOp",EDGE,"E22.left"),sQuery(id+"F1.wireOp",EDGE,"E22.right"),sQuery(id+"F1.wireOp",EDGE,"E23.bottom"),sQuery(id+"F1.wireOp",EDGE,"E23.top"),sQuery(id+"F1.wireOp",EDGE,"E23.left"),sQuery(id+"F1.wireOp",EDGE,"E23.right"),sQuery(id+"F1.wireOp",EDGE,"E38"),sQuery(id+"F1.wireOp",EDGE,"E39"),sQuery(id+"F1.wireOp",EDGE,"E40"),sQuery(id+"F1.wireOp",EDGE,"E41")])],"isStart":false}),makeQuery(id+"F4.opExtrude","SWEPT_FACE",FACE,{"disambiguationData":[OSD([sQuery(id+"F0.wireOp",EDGE,"E3.bottom")])]})]});
            var Q8;
            Q8=makeQuery(id+"F4.boolean.opBoolean","INTERSECT",EDGE,{"derivedFrom":[makeQuery(id+"F2.opExtrude","CAP_FACE",FACE,{"disambiguationData":[OSD([sQuery(id+"F1.wireOp",EDGE,"E22.left"),sQuery(id+"F1.wireOp",EDGE,"E22.right"),sQuery(id+"F1.wireOp",EDGE,"E23.bottom"),sQuery(id+"F1.wireOp",EDGE,"E23.top"),sQuery(id+"F1.wireOp",EDGE,"E23.left"),sQuery(id+"F1.wireOp",EDGE,"E23.right"),sQuery(id+"F1.wireOp",EDGE,"E38"),sQuery(id+"F1.wireOp",EDGE,"E39"),sQuery(id+"F1.wireOp",EDGE,"E40"),sQuery(id+"F1.wireOp",EDGE,"E41")])],"isStart":false}),makeQuery(id+"F4.opExtrude","SWEPT_FACE",FACE,{"disambiguationData":[OSD([sQuery(id+"F0.wireOp",EDGE,"E7.left")])]})]});
            var Q9;
            Q9=makeQuery(id+"F4.boolean.opBoolean","INTERSECT",EDGE,{"derivedFrom":[makeQuery(id+"F2.opExtrude","CAP_FACE",FACE,{"disambiguationData":[OSD([sQuery(id+"F1.wireOp",EDGE,"E22.left"),sQuery(id+"F1.wireOp",EDGE,"E22.right"),sQuery(id+"F1.wireOp",EDGE,"E23.bottom"),sQuery(id+"F1.wireOp",EDGE,"E23.top"),sQuery(id+"F1.wireOp",EDGE,"E23.left"),sQuery(id+"F1.wireOp",EDGE,"E23.right"),sQuery(id+"F1.wireOp",EDGE,"E38"),sQuery(id+"F1.wireOp",EDGE,"E39"),sQuery(id+"F1.wireOp",EDGE,"E40"),sQuery(id+"F1.wireOp",EDGE,"E41")])],"isStart":false}),makeQuery(id+"F4.opExtrude","SWEPT_FACE",FACE,{"disambiguationData":[OSD([sQuery(id+"F0.wireOp",EDGE,"E9.left")])]})]});
            var Q10;
            Q10=makeQuery(id+"F4.boolean.opBoolean","INTERSECT",EDGE,{"derivedFrom":[makeQuery(id+"F2.opExtrude","CAP_FACE",FACE,{"disambiguationData":[OSD([sQuery(id+"F1.wireOp",EDGE,"E22.left"),sQuery(id+"F1.wireOp",EDGE,"E22.right"),sQuery(id+"F1.wireOp",EDGE,"E23.bottom"),sQuery(id+"F1.wireOp",EDGE,"E23.top"),sQuery(id+"F1.wireOp",EDGE,"E23.left"),sQuery(id+"F1.wireOp",EDGE,"E23.right"),sQuery(id+"F1.wireOp",EDGE,"E38"),sQuery(id+"F1.wireOp",EDGE,"E39"),sQuery(id+"F1.wireOp",EDGE,"E40"),sQuery(id+"F1.wireOp",EDGE,"E41")])],"isStart":false}),makeQuery(id+"F4.opExtrude","SWEPT_FACE",FACE,{"disambiguationData":[OSD([sQuery(id+"F0.wireOp",EDGE,"E1.left")])]})]});
            var Q11;
            Q11=makeQuery(id+"F4.boolean.opBoolean","INTERSECT",EDGE,{"derivedFrom":[makeQuery(id+"F2.opExtrude","CAP_FACE",FACE,{"disambiguationData":[OSD([sQuery(id+"F1.wireOp",EDGE,"E22.left"),sQuery(id+"F1.wireOp",EDGE,"E22.right"),sQuery(id+"F1.wireOp",EDGE,"E23.bottom"),sQuery(id+"F1.wireOp",EDGE,"E23.top"),sQuery(id+"F1.wireOp",EDGE,"E23.left"),sQuery(id+"F1.wireOp",EDGE,"E23.right"),sQuery(id+"F1.wireOp",EDGE,"E38"),sQuery(id+"F1.wireOp",EDGE,"E39"),sQuery(id+"F1.wireOp",EDGE,"E40"),sQuery(id+"F1.wireOp",EDGE,"E41")])],"isStart":false}),makeQuery(id+"F4.opExtrude","SWEPT_FACE",FACE,{"disambiguationData":[OSD([sQuery(id+"F0.wireOp",EDGE,"E5.right")])]})]});
            var Q12;
            Q12=makeQuery(id+"F4.boolean.opBoolean","INTERSECT",EDGE,{"derivedFrom":[makeQuery(id+"F2.opExtrude","CAP_FACE",FACE,{"disambiguationData":[OSD([sQuery(id+"F1.wireOp",EDGE,"E22.left"),sQuery(id+"F1.wireOp",EDGE,"E22.right"),sQuery(id+"F1.wireOp",EDGE,"E23.bottom"),sQuery(id+"F1.wireOp",EDGE,"E23.top"),sQuery(id+"F1.wireOp",EDGE,"E23.left"),sQuery(id+"F1.wireOp",EDGE,"E23.right"),sQuery(id+"F1.wireOp",EDGE,"E38"),sQuery(id+"F1.wireOp",EDGE,"E39"),sQuery(id+"F1.wireOp",EDGE,"E40"),sQuery(id+"F1.wireOp",EDGE,"E41")])],"isStart":false}),makeQuery(id+"F4.opExtrude","SWEPT_FACE",FACE,{"disambiguationData":[OSD([sQuery(id+"F0.wireOp",EDGE,"E6.right")])]})]});
            var Q13;
            Q13=makeQuery(id+"F4.boolean.opBoolean","INTERSECT",EDGE,{"derivedFrom":[makeQuery(id+"F2.opExtrude","CAP_FACE",FACE,{"disambiguationData":[OSD([sQuery(id+"F1.wireOp",EDGE,"E22.left"),sQuery(id+"F1.wireOp",EDGE,"E22.right"),sQuery(id+"F1.wireOp",EDGE,"E23.bottom"),sQuery(id+"F1.wireOp",EDGE,"E23.top"),sQuery(id+"F1.wireOp",EDGE,"E23.left"),sQuery(id+"F1.wireOp",EDGE,"E23.right"),sQuery(id+"F1.wireOp",EDGE,"E38"),sQuery(id+"F1.wireOp",EDGE,"E39"),sQuery(id+"F1.wireOp",EDGE,"E40"),sQuery(id+"F1.wireOp",EDGE,"E41")])],"isStart":false}),makeQuery(id+"F4.opExtrude","SWEPT_FACE",FACE,{"disambiguationData":[OSD([sQuery(id+"F0.wireOp",EDGE,"E4.right")])]})]});
            var Q14;
            Q14=makeQuery(id+"F4.boolean.opBoolean","INTERSECT",EDGE,{"derivedFrom":[makeQuery(id+"F2.opExtrude","CAP_FACE",FACE,{"disambiguationData":[OSD([sQuery(id+"F1.wireOp",EDGE,"E22.left"),sQuery(id+"F1.wireOp",EDGE,"E22.right"),sQuery(id+"F1.wireOp",EDGE,"E23.bottom"),sQuery(id+"F1.wireOp",EDGE,"E23.top"),sQuery(id+"F1.wireOp",EDGE,"E23.left"),sQuery(id+"F1.wireOp",EDGE,"E23.right"),sQuery(id+"F1.wireOp",EDGE,"E38"),sQuery(id+"F1.wireOp",EDGE,"E39"),sQuery(id+"F1.wireOp",EDGE,"E40"),sQuery(id+"F1.wireOp",EDGE,"E41")])],"isStart":false}),makeQuery(id+"F4.opExtrude","SWEPT_FACE",FACE,{"disambiguationData":[OSD([sQuery(id+"F0.wireOp",EDGE,"E4.bottom")])]})]});
            var Q15;
            Q15=makeQuery(id+"F4.boolean.opBoolean","INTERSECT",EDGE,{"derivedFrom":[makeQuery(id+"F2.opExtrude","CAP_FACE",FACE,{"disambiguationData":[OSD([sQuery(id+"F1.wireOp",EDGE,"E22.left"),sQuery(id+"F1.wireOp",EDGE,"E22.right"),sQuery(id+"F1.wireOp",EDGE,"E23.bottom"),sQuery(id+"F1.wireOp",EDGE,"E23.top"),sQuery(id+"F1.wireOp",EDGE,"E23.left"),sQuery(id+"F1.wireOp",EDGE,"E23.right"),sQuery(id+"F1.wireOp",EDGE,"E38"),sQuery(id+"F1.wireOp",EDGE,"E39"),sQuery(id+"F1.wireOp",EDGE,"E40"),sQuery(id+"F1.wireOp",EDGE,"E41")])],"isStart":false}),makeQuery(id+"F4.opExtrude","SWEPT_FACE",FACE,{"disambiguationData":[OSD([sQuery(id+"F0.wireOp",EDGE,"E3.right")])]})]});
            var Q16;
            Q16=makeQuery(id+"F4.boolean.opBoolean","INTERSECT",EDGE,{"derivedFrom":[makeQuery(id+"F2.opExtrude","CAP_FACE",FACE,{"disambiguationData":[OSD([sQuery(id+"F1.wireOp",EDGE,"E22.left"),sQuery(id+"F1.wireOp",EDGE,"E22.right"),sQuery(id+"F1.wireOp",EDGE,"E23.bottom"),sQuery(id+"F1.wireOp",EDGE,"E23.top"),sQuery(id+"F1.wireOp",EDGE,"E23.left"),sQuery(id+"F1.wireOp",EDGE,"E23.right"),sQuery(id+"F1.wireOp",EDGE,"E38"),sQuery(id+"F1.wireOp",EDGE,"E39"),sQuery(id+"F1.wireOp",EDGE,"E40"),sQuery(id+"F1.wireOp",EDGE,"E41")])],"isStart":false}),makeQuery(id+"F4.opExtrude","SWEPT_FACE",FACE,{"disambiguationData":[OSD([sQuery(id+"F0.wireOp",EDGE,"E6.top"),sQuery(id+"F0.wireOp",EDGE,"E7.top")])]})]});
            var Q17;
            Q17=makeQuery(id+"F4.boolean.opBoolean","INTERSECT",EDGE,{"derivedFrom":[makeQuery(id+"F2.opExtrude","CAP_FACE",FACE,{"disambiguationData":[OSD([sQuery(id+"F1.wireOp",EDGE,"E22.left"),sQuery(id+"F1.wireOp",EDGE,"E22.right"),sQuery(id+"F1.wireOp",EDGE,"E23.bottom"),sQuery(id+"F1.wireOp",EDGE,"E23.top"),sQuery(id+"F1.wireOp",EDGE,"E23.left"),sQuery(id+"F1.wireOp",EDGE,"E23.right"),sQuery(id+"F1.wireOp",EDGE,"E38"),sQuery(id+"F1.wireOp",EDGE,"E39"),sQuery(id+"F1.wireOp",EDGE,"E40"),sQuery(id+"F1.wireOp",EDGE,"E41")])],"isStart":false}),makeQuery(id+"F4.opExtrude","SWEPT_FACE",FACE,{"disambiguationData":[OSD([sQuery(id+"F0.wireOp",EDGE,"E3.left")])]})]});
            var Q18;
            Q18=makeQuery(id+"F4.boolean.opBoolean","INTERSECT",EDGE,{"derivedFrom":[makeQuery(id+"F2.opExtrude","CAP_FACE",FACE,{"disambiguationData":[OSD([sQuery(id+"F1.wireOp",EDGE,"E22.left"),sQuery(id+"F1.wireOp",EDGE,"E22.right"),sQuery(id+"F1.wireOp",EDGE,"E23.bottom"),sQuery(id+"F1.wireOp",EDGE,"E23.top"),sQuery(id+"F1.wireOp",EDGE,"E23.left"),sQuery(id+"F1.wireOp",EDGE,"E23.right"),sQuery(id+"F1.wireOp",EDGE,"E38"),sQuery(id+"F1.wireOp",EDGE,"E39"),sQuery(id+"F1.wireOp",EDGE,"E40"),sQuery(id+"F1.wireOp",EDGE,"E41")])],"isStart":false}),makeQuery(id+"F4.opExtrude","SWEPT_FACE",FACE,{"disambiguationData":[OSD([sQuery(id+"F0.wireOp",EDGE,"E3.top")])]})]});
            var Q19;
            Q19=makeQuery(id+"F4.boolean.opBoolean","INTERSECT",EDGE,{"derivedFrom":[makeQuery(id+"F2.opExtrude","CAP_FACE",FACE,{"disambiguationData":[OSD([sQuery(id+"F1.wireOp",EDGE,"E22.left"),sQuery(id+"F1.wireOp",EDGE,"E22.right"),sQuery(id+"F1.wireOp",EDGE,"E23.bottom"),sQuery(id+"F1.wireOp",EDGE,"E23.top"),sQuery(id+"F1.wireOp",EDGE,"E23.left"),sQuery(id+"F1.wireOp",EDGE,"E23.right"),sQuery(id+"F1.wireOp",EDGE,"E38"),sQuery(id+"F1.wireOp",EDGE,"E39"),sQuery(id+"F1.wireOp",EDGE,"E40"),sQuery(id+"F1.wireOp",EDGE,"E41")])],"isStart":false}),makeQuery(id+"F4.opExtrude","SWEPT_FACE",FACE,{"disambiguationData":[OSD([sQuery(id+"F0.wireOp",EDGE,"E1.top")])]})]});
            var Q20;
            Q20=makeQuery(id+"F4.boolean.opBoolean","INTERSECT",EDGE,{"derivedFrom":[makeQuery(id+"F2.opExtrude","CAP_FACE",FACE,{"disambiguationData":[OSD([sQuery(id+"F1.wireOp",EDGE,"E22.left"),sQuery(id+"F1.wireOp",EDGE,"E22.right"),sQuery(id+"F1.wireOp",EDGE,"E23.bottom"),sQuery(id+"F1.wireOp",EDGE,"E23.top"),sQuery(id+"F1.wireOp",EDGE,"E23.left"),sQuery(id+"F1.wireOp",EDGE,"E23.right"),sQuery(id+"F1.wireOp",EDGE,"E38"),sQuery(id+"F1.wireOp",EDGE,"E39"),sQuery(id+"F1.wireOp",EDGE,"E40"),sQuery(id+"F1.wireOp",EDGE,"E41")])],"isStart":false}),makeQuery(id+"F4.opExtrude","SWEPT_FACE",FACE,{"disambiguationData":[OSD([sQuery(id+"F0.wireOp",EDGE,"E1.right")])]})]});
            var Q21;
            Q21=makeQuery(id+"F4.boolean.opBoolean","INTERSECT",EDGE,{"derivedFrom":[makeQuery(id+"F2.opExtrude","CAP_FACE",FACE,{"disambiguationData":[OSD([sQuery(id+"F1.wireOp",EDGE,"E22.left"),sQuery(id+"F1.wireOp",EDGE,"E22.right"),sQuery(id+"F1.wireOp",EDGE,"E23.bottom"),sQuery(id+"F1.wireOp",EDGE,"E23.top"),sQuery(id+"F1.wireOp",EDGE,"E23.left"),sQuery(id+"F1.wireOp",EDGE,"E23.right"),sQuery(id+"F1.wireOp",EDGE,"E38"),sQuery(id+"F1.wireOp",EDGE,"E39"),sQuery(id+"F1.wireOp",EDGE,"E40"),sQuery(id+"F1.wireOp",EDGE,"E41")])],"isStart":false}),makeQuery(id+"F4.opExtrude","SWEPT_FACE",FACE,{"disambiguationData":[OSD([sQuery(id+"F0.wireOp",EDGE,"E5.top"),sQuery(id+"F0.wireOp",EDGE,"E9.top")])]})]});
            var Q22;
            Q22=makeQuery(id+"F4.boolean.opBoolean","INTERSECT",EDGE,{"derivedFrom":[makeQuery(id+"F2.opExtrude","CAP_FACE",FACE,{"disambiguationData":[OSD([sQuery(id+"F1.wireOp",EDGE,"E22.left"),sQuery(id+"F1.wireOp",EDGE,"E22.right"),sQuery(id+"F1.wireOp",EDGE,"E23.bottom"),sQuery(id+"F1.wireOp",EDGE,"E23.top"),sQuery(id+"F1.wireOp",EDGE,"E23.left"),sQuery(id+"F1.wireOp",EDGE,"E23.right"),sQuery(id+"F1.wireOp",EDGE,"E38"),sQuery(id+"F1.wireOp",EDGE,"E39"),sQuery(id+"F1.wireOp",EDGE,"E40"),sQuery(id+"F1.wireOp",EDGE,"E41")])],"isStart":false}),makeQuery(id+"F4.opExtrude","SWEPT_FACE",FACE,{"disambiguationData":[OSD([sQuery(id+"F0.wireOp",EDGE,"E4.top")])]})]});
            var Q23;
            Q23=makeQuery(id+"F4.boolean.opBoolean","INTERSECT",EDGE,{"derivedFrom":[makeQuery(id+"F2.opExtrude","CAP_FACE",FACE,{"disambiguationData":[OSD([sQuery(id+"F1.wireOp",EDGE,"E22.left"),sQuery(id+"F1.wireOp",EDGE,"E22.right"),sQuery(id+"F1.wireOp",EDGE,"E23.bottom"),sQuery(id+"F1.wireOp",EDGE,"E23.top"),sQuery(id+"F1.wireOp",EDGE,"E23.left"),sQuery(id+"F1.wireOp",EDGE,"E23.right"),sQuery(id+"F1.wireOp",EDGE,"E38"),sQuery(id+"F1.wireOp",EDGE,"E39"),sQuery(id+"F1.wireOp",EDGE,"E40"),sQuery(id+"F1.wireOp",EDGE,"E41")])],"isStart":false}),makeQuery(id+"F4.opExtrude","SWEPT_FACE",FACE,{"disambiguationData":[OSD([sQuery(id+"F0.wireOp",EDGE,"E4.left")])]})]});
            fillet(context, id + "F6", {"entities" : qUnion([Q0, Q1, Q2, Q3, Q4, Q5, Q6, Q7, Q8, Q9, Q10, Q11, Q12, Q13, Q14, Q15, Q16, Q17, Q18, Q19, Q20, Q21, Q22, Q23]), "radius" : 2 * mm, "tangentPropagation" : true, "allowEdgeOverflow" : false});
        }
        {
            var Q0;
            {var subQ0=sQuery(id+"F1.wireOp",EDGE,"E54");var subQ1=sQuery(id+"F1.wireOp",EDGE,"E36");var subQ2=makeQuery(id+"F1.imprint","INTERSECT",VERTEX,{"derivedFrom":[subQ1,subQ0]});Q0=makeQuery(id+"F1.imprint","IMPRINT",FACE,{"disambiguationData":[TD([[makeQuery(id+"F1.imprint","IMPRINT",EDGE,{"disambiguationData":[TD([[subQ2,-1.0]])],"derivedFrom":subQ1}),1.0]])]});}
            extrude(context, id + "F7", {"entities" : qUnion([Q0]), "operationType" : NewBodyOperationType.ADD, "depth" : 1 * mm, "offsetDistance" : 25 * mm});
        }
    });
